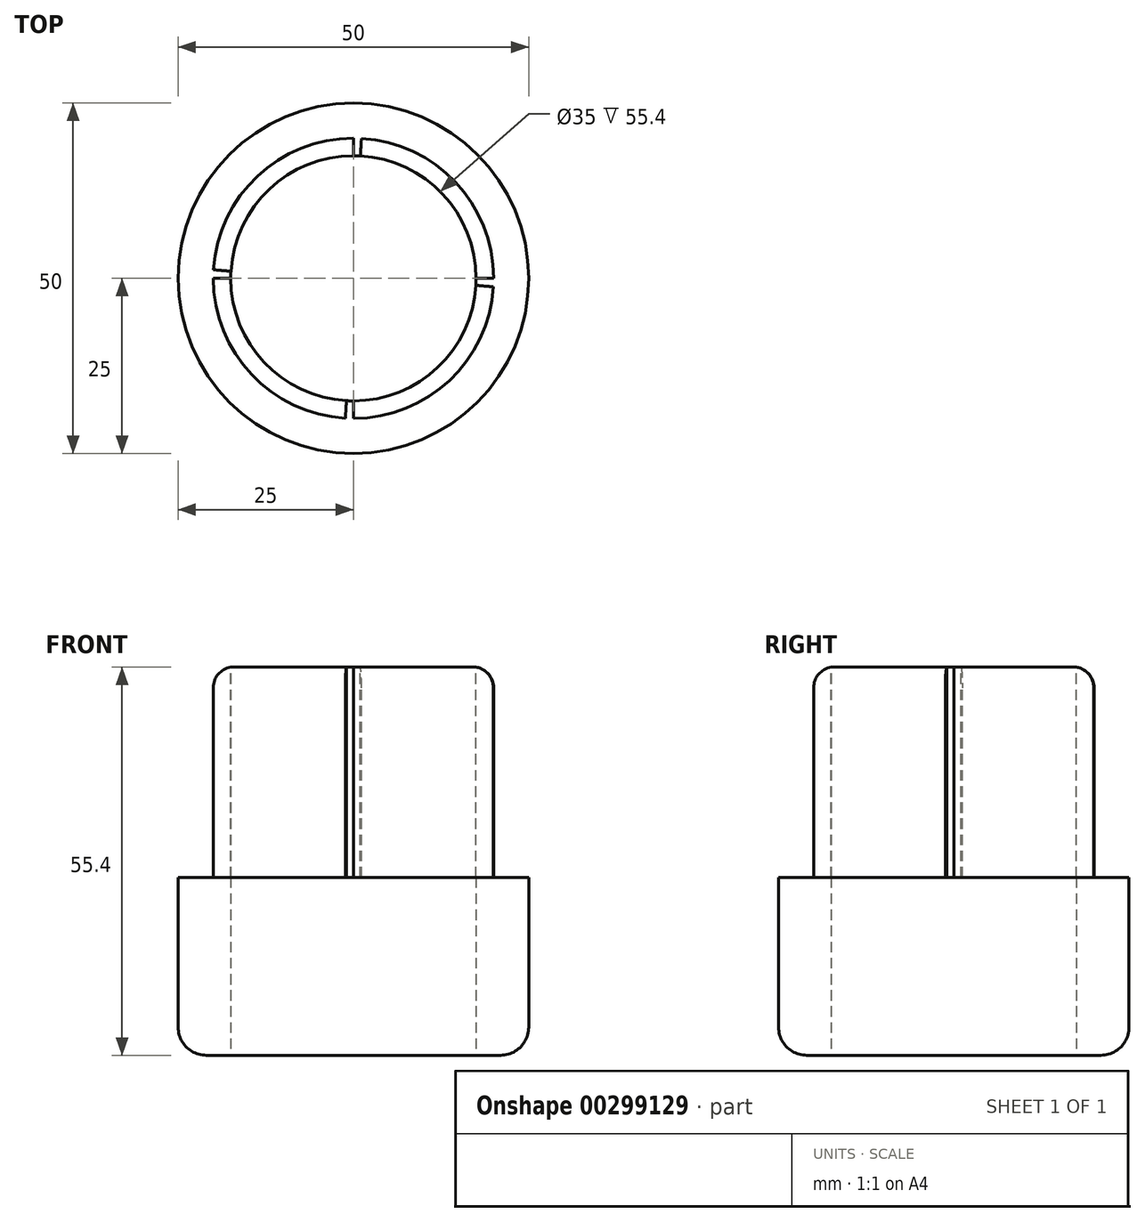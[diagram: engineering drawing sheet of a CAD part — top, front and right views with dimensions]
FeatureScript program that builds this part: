
annotation { "Feature Type Name" : "Feature", "Feature Type Description" : "" }
export const myFeature = defineFeature(function(context is Context, id is Id, definition is map)
    precondition{}
    {
        {
            var Q0;
            Q0=qCreatedBy(makeId("Top.planeOp"),FACE);
            var sketch = newSketch(context, id + "F0", { "sketchPlane" : qUnion([Q0])});
            skCircle(sketch, "E0", {"center": v(0, 0) * mm, "radius": 25 * mm});
            skCircle(sketch, "E1", {"center": v(0, 0) * mm, "radius": 20 * mm});
            skCircle(sketch, "E2", {"center": v(0, 0) * mm, "radius": 17.5 * mm});
            skSolve(sketch);
        }
        {
            var Q0;
            Q0 = qSketchRegion(id + "F0", true);
            var Q1;
            Q1=makeQuery(id+"F0.imprint","IMPRINT",FACE,{"disambiguationData":[TD([[makeQuery(id+"F0.imprint","IMPRINT",EDGE,{"derivedFrom":sQuery(id+"F0.wireOp",EDGE,"E1")}),1.0]])]});
            extrude(context, id + "F1", {"entities" : qUnion([Q0, Q1]), "depth" : 25.4 * mm});
        }
        {
            var Q0;
            Q0=makeQuery(id+"F0.imprint","IMPRINT",FACE,{"disambiguationData":[TD([[makeQuery(id+"F0.imprint","IMPRINT",EDGE,{"derivedFrom":sQuery(id+"F0.wireOp",EDGE,"E1")}),1.0]])]});
            extrude(context, id + "F2", {"entities" : qUnion([Q0]), "operationType" : NewBodyOperationType.ADD, "depth" : 55.4 * mm});
        }
        {
            var Q0;
            Q0=makeQuery(id+"F2.opExtrude","CAP_FACE",FACE,{"disambiguationData":[OSD([sQuery(id+"F0.wireOp",EDGE,"E1"),sQuery(id+"F0.wireOp",EDGE,"E2")])],"isStart":false});
            var sketch = newSketch(context, id + "F3", { "sketchPlane" : qUnion([Q0])});
            skLineSegment(sketch, "E3", {"start": v(0, 17.5) * mm, "end": v(0, 20) * mm});
            skLineSegment(sketch, "E4", {"start": v(0, -17.5) * mm, "end": v(0, -20) * mm});
            skLineSegment(sketch, "E5", {"start": v(-17.5, 0) * mm, "end": v(-20, 0) * mm});
            skLineSegment(sketch, "E6", {"start": v(17.5, 0) * mm, "end": v(20, 0) * mm});
            skPoint(sketch, "E7", {"position": v(1, 17.47) * mm});
            skPoint(sketch, "E8", {"position": v(0, 17.5) * mm});
            skLineSegment(sketch, "E9", {"start": v(0, 17.5) * mm, "end": v(1, 17.47) * mm, "construction": true});
            skLineSegment(sketch, "E10", {"start": v(17.5, 0) * mm, "end": v(17.47, -1) * mm, "construction": true});
            skLineSegment(sketch, "E11", {"start": v(-17.5, 0) * mm, "end": v(-17.47, 1) * mm, "construction": true});
            skLineSegment(sketch, "E12", {"start": v(0, -17.5) * mm, "end": v(-1, -17.47) * mm, "construction": true});
            skLineSegment(sketch, "E13", {"start": v(1, 17.47) * mm, "end": v(1.14, 19.97) * mm});
            skLineSegment(sketch, "E14.MirrorCS", {"start": v(-1, -17.47) * mm, "end": v(-1.14, -19.97) * mm});
            skLineSegment(sketch, "E15", {"start": v(17.47, -1) * mm, "end": v(19.96, -1.22) * mm});
            skLineSegment(sketch, "E16.MirrorCS", {"start": v(-17.47, 1) * mm, "end": v(-19.96, 1.22) * mm});
            skSolve(sketch);
        }
        {
            var Q0;
            {var subQ0=sQuery(id+"F3.wireOp",EDGE,"E3");Q0=makeQuery(id+"F3.imprint","IMPRINT",FACE,{"disambiguationData":[TD([[makeQuery(id+"F3.imprint","IMPRINT",EDGE,{"derivedFrom":subQ0}),-1.0]])]});}
            var Q1;
            {var subQ0=sQuery(id+"F3.wireOp",EDGE,"E6");Q1=makeQuery(id+"F3.imprint","IMPRINT",FACE,{"disambiguationData":[TD([[makeQuery(id+"F3.imprint","IMPRINT",EDGE,{"derivedFrom":subQ0}),-1.0]])]});}
            var Q2;
            {var subQ0=sQuery(id+"F3.wireOp",EDGE,"E5");Q2=makeQuery(id+"F3.imprint","IMPRINT",FACE,{"disambiguationData":[TD([[makeQuery(id+"F3.imprint","IMPRINT",EDGE,{"derivedFrom":subQ0}),-1.0]])]});}
            var Q3;
            {var subQ0=sQuery(id+"F3.wireOp",EDGE,"E4");Q3=makeQuery(id+"F3.imprint","IMPRINT",FACE,{"disambiguationData":[TD([[makeQuery(id+"F3.imprint","IMPRINT",EDGE,{"derivedFrom":subQ0}),-1.0]])]});}
            extrude(context, id + "F4", {"entities" : qUnion([Q0, Q1, Q2, Q3]), "operationType" : NewBodyOperationType.REMOVE, "oppositeDirection" : true, "depth" : 30 * mm});
        }
        {
            var Q0;
            {var subQ0=sQuery(id+"F0.wireOp",EDGE,"E1");Q0=makeQuery(id+"F4.boolean.opBoolean","SPLIT",EDGE,{"disambiguationData":[TD([makeQuery(id+"F4.opExtrude","SWEPT_FACE",FACE,{"disambiguationData":[OSD([sQuery(id+"F3.wireOp",EDGE,"E3")])]})])],"derivedFrom":makeQuery(id+"F2.opExtrude","CAP_EDGE",EDGE,{"disambiguationData":[OSD([subQ0])],"isStart":false})});}
            var Q1;
            {var subQ0=sQuery(id+"F0.wireOp",EDGE,"E1");Q1=makeQuery(id+"F4.boolean.opBoolean","SPLIT",EDGE,{"disambiguationData":[TD([makeQuery(id+"F4.opExtrude","SWEPT_FACE",FACE,{"disambiguationData":[OSD([sQuery(id+"F3.wireOp",EDGE,"E5")])]})])],"derivedFrom":makeQuery(id+"F2.opExtrude","CAP_EDGE",EDGE,{"disambiguationData":[OSD([subQ0])],"isStart":false})});}
            var Q2;
            {var subQ0=sQuery(id+"F0.wireOp",EDGE,"E1");Q2=makeQuery(id+"F4.boolean.opBoolean","SPLIT",EDGE,{"disambiguationData":[TD([makeQuery(id+"F4.opExtrude","SWEPT_FACE",FACE,{"disambiguationData":[OSD([sQuery(id+"F3.wireOp",EDGE,"E4")])]})])],"derivedFrom":makeQuery(id+"F2.opExtrude","CAP_EDGE",EDGE,{"disambiguationData":[OSD([subQ0])],"isStart":false})});}
            var Q3;
            {var subQ0=sQuery(id+"F0.wireOp",EDGE,"E1");Q3=makeQuery(id+"F4.boolean.opBoolean","SPLIT",EDGE,{"disambiguationData":[TD([makeQuery(id+"F4.opExtrude","SWEPT_FACE",FACE,{"disambiguationData":[OSD([sQuery(id+"F3.wireOp",EDGE,"E6")])]})])],"derivedFrom":makeQuery(id+"F2.opExtrude","CAP_EDGE",EDGE,{"disambiguationData":[OSD([subQ0])],"isStart":false})});}
            fillet(context, id + "F5", {"entities" : qUnion([Q0, Q1, Q2, Q3]), "radius" : 3 * mm, "tangentPropagation" : true, "allowEdgeOverflow" : false});
        }
        {
            var Q0;
            Q0=makeQuery(id+"F1.opExtrude","CAP_EDGE",EDGE,{"disambiguationData":[OSD([sQuery(id+"F0.wireOp",EDGE,"E0")])],"isStart":true});
            fillet(context, id + "F6", {"entities" : qUnion([Q0]), "radius" : 4 * mm, "tangentPropagation" : true, "allowEdgeOverflow" : false});
        }
    });
